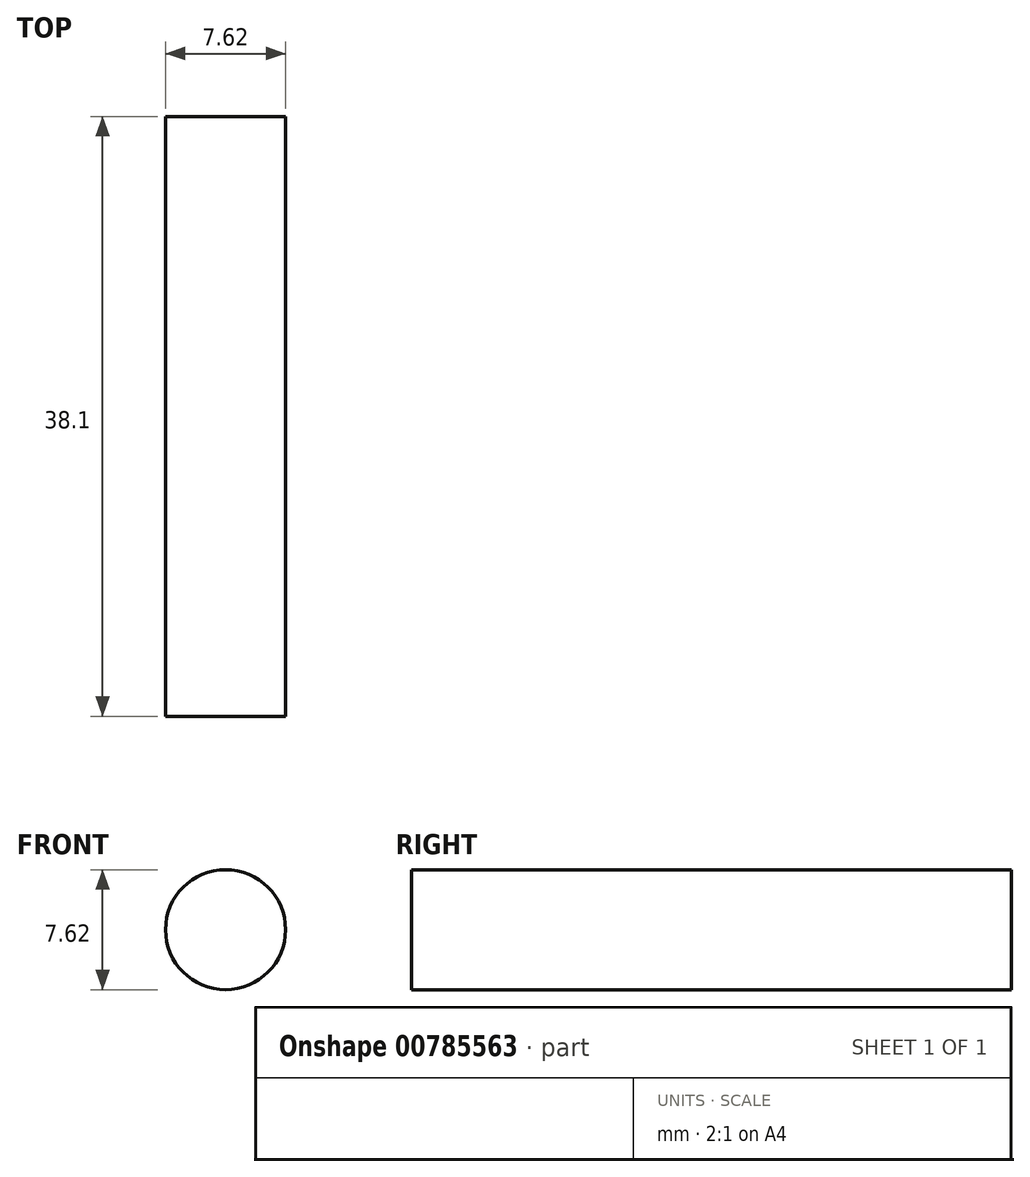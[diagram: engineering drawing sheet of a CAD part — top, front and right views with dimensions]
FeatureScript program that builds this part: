
annotation { "Feature Type Name" : "Feature", "Feature Type Description" : "" }
export const myFeature = defineFeature(function(context is Context, id is Id, definition is map)
    precondition{}
    {
        {
            var Q0;
            Q0=qCreatedBy(makeId("Front.planeOp"),FACE);
            var sketch = newSketch(context, id + "F0", { "sketchPlane" : qUnion([Q0])});
            skCircle(sketch, "E0", {"center": v(0, 0) * mm, "radius": 3.81 * mm});
            skSolve(sketch);
        }
        {
            var Q0;
            Q0 = qSketchRegion(id + "F0", true);
            extrude(context, id + "F1", {"entities" : qUnion([Q0]), "depth" : 38.1 * mm, "offsetDistance" : 25.4 * mm});
        }
    });
